# Revit family: ledwallspot-e_rd60-10w-840-24d-bl_715000002600
name_source: partatom
category: Leuchten
revit_build: Autodesk Revit 2016 (Build: 20190508_0715(x64)
units: mm (PartAtom-declared; Revit-internal decimal feet)

## family parameters
Basisbauteil = Fläche
Beim Laden mit Abzugskörper schneiden = Nein
Bemaßung runder Anschluss = Durchmesser verwenden
Gemeinsam genutzt = Nein
Lichtquelle = Nein
Raumberechnungspunkt = Nein
Teiletyp = Normal

## types (1)
- LEDWallSpot-E Rd60-10W-840-24D-BL (1 x LED, 800 lm)
    Approval mark = CE, ENEC
    Beschreibung = Up and down accent lighting suitable for modern architecture. IP65 water resistance level with strong impact protection of IK06. Corrosion-resistant die-cast aluminium body with no visible screws (stainless steel). Easy loop-in and loop-out installation. Different beam angles available via refector accessories. Broad applications including both commercial and residential areas. IP65 and suitable for use on the coastal applications.
    CIE Flux Codes = 99 100 100 50 100
    Control Gear = Electronic ballast
    Height = 170 mm  [stored 0.557743 ft]
    Hersteller = OPPLE
    Lamp Light Flux = 800 lm
    Lamp count = 1
    Lampe = 1 x LED
    Length = 60 mm  [stored 0.19685 ft]
    Luminous efficacy = 80 lm/W
    ModVariant = Nein
    Modell = 715000002600
    Mounting Place = Wall
    Mounting Type = Surface mounted
    Number of Poles = 1
    OnlyDefault = Ja
    Power Factor = 1
    Product Name = LEDWallSpot-E Rd60-10W-840-24D-BL
    Product group = Wall Spot
    ProductGroupID = 2020
    Protection Class = Protection class I
    Protection Degree = IP 65
    RLX_Detail_Level = 1
    RlxData = <blob elided: 155261 chars, md5=148c3399>
    Scheinlast = 10 VA
    Socket = socket
    Standby Power = 0 W
    System Light Flux = 799 lm
    System Power = 10 W
    Typenbild = 715000002600.jpg
    Typenkommentare = Product without accessories
    URL = http://relux.com
    VarID = ---
    Voltage = 0 V
    Vorgabe-Ansicht = 1800 mm
    Weight = 0.00 kg
    Width = 0 mm  [stored 0 ft]

note: [stored X ft] marks values corroborated as IEEE doubles in the binary element streams (Revit-internal decimal feet)

## geometry (parser evidence)
native form markers: Blend x4, Sweep x13
no freeform markers — native parametric forms only
